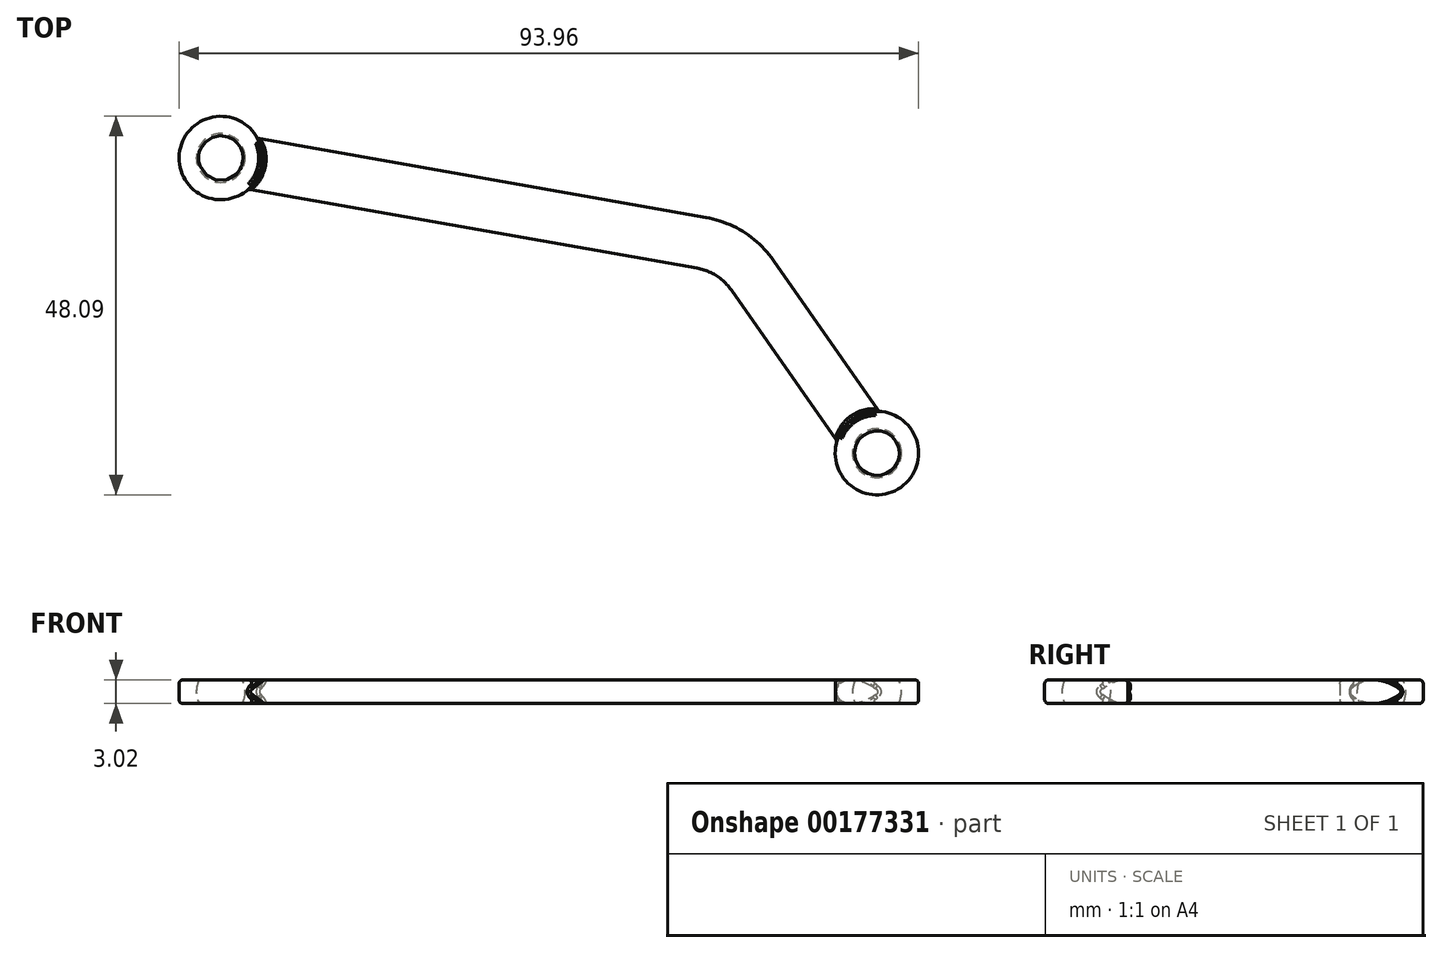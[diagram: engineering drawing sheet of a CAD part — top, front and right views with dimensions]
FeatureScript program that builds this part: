
annotation { "Feature Type Name" : "Feature", "Feature Type Description" : "" }
export const myFeature = defineFeature(function(context is Context, id is Id, definition is map)
    precondition{}
    {
        {
            var Q0;
            Q0=qCreatedBy(makeId("Top.planeOp"),FACE);
            var sketch = newSketch(context, id + "F0", { "sketchPlane" : qUnion([Q0])});
            skLineSegment(sketch, "E0", {"start": v(0, 0) * mm, "end": v(-15.83, 22.6) * mm});
            skLineSegment(sketch, "E1", {"start": v(-22.28, 26.72) * mm, "end": v(-83.36, 37.49) * mm});
            skPoint(sketch, "E2.visualSharp", {"position": v(-18.2, 26) * mm});
            skArc(sketch, "E2.filletArc", {"start": v(-15.83, 22.6) * mm, "mid": v(-18.65, 25.3) * mm, "end": v(-22.28, 26.72) * mm});
            skSolve(sketch);
        }
        {
            var Q0;
            Q0=qCreatedBy(makeId("Top.planeOp"),FACE);
            var sketch = newSketch(context, id + "F1", { "sketchPlane" : qUnion([Q0])});
            skLineSegment(sketch, "E3", {"start": v(-31.75, -22.23) * mm, "end": v(29.07, 20.36) * mm});
            skSolve(sketch);
        }
        {
            var Q0;
            Q0=sQuery(id+"F1.wireOp",EDGE,"E3");
            cPlane(context, id + "F2", {"entities" : qUnion([Q0]), "cplaneType" : CPlaneType.LINE_ANGLE, "offset" : 25 * mm, "angle" : 0 * degree, "width" : 150 * mm, "height" : 150 * mm});
        }
        {
            var Q0;
            Q0=qCreatedBy(id+"F2.planeOp",FACE);
            var sketch = newSketch(context, id + "F3", { "sketchPlane" : qUnion([Q0])});
            skArc(sketch, "E4", {"start": v(3.5, 0) * mm, "mid": v(0, 1.5) * mm, "end": v(-3.5, 0) * mm});
            skArc(sketch, "E5.MirrorCS", {"start": v(3.5, 0) * mm, "mid": v(0, -1.5) * mm, "end": v(-3.5, 0) * mm});
            skSolve(sketch);
        }
        {
            var Q0;
            Q0=makeQuery(id+"F3.imprint","IMPRINT",FACE,{"disambiguationData":[TD([[makeQuery(id+"F3.imprint","IMPRINT",EDGE,{"derivedFrom":sQuery(id+"F3.wireOp",EDGE,"E4")}),1.0]])]});
            var Q1;
            Q1=sQuery(id+"F0.wireOp",EDGE,"E0");
            var Q2;
            Q2=sQuery(id+"F0.wireOp",EDGE,"E2.filletArc");
            var Q3;
            Q3=sQuery(id+"F0.wireOp",EDGE,"E1");
            sweep(context, id + "F4", {"profiles" : qUnion([Q0]), "path" : qUnion([Q1, Q2, Q3])});
        }
        {
            var Q0;
            Q0=qCreatedBy(makeId("Top.planeOp"),FACE);
            var sketch = newSketch(context, id + "F5", { "sketchPlane" : qUnion([Q0])});
            skCircle(sketch, "E6", {"center": v(0, 0) * mm, "radius": 5.3 * mm});
            skCircle(sketch, "E7", {"center": v(-83.36, 37.49) * mm, "radius": 5.3 * mm});
            skSolve(sketch);
        }
        {
            var Q0;
            Q0 = qSketchRegion(id + "F5", true);
            extrude(context, id + "F6", {"entities" : qUnion([Q0]), "operationType" : NewBodyOperationType.ADD, "depth" : 3 * mm, "offsetDistance" : 25 * mm, "symmetric" : true});
        }
        {
            var Q0;
            Q0=qCreatedBy(id+"F2.planeOp",FACE);
            var sketch = newSketch(context, id + "F7", { "sketchPlane" : qUnion([Q0])});
            skLineSegment(sketch, "E8", {"start": v(0, 3.1) * mm, "end": v(0, -3.1) * mm});
            skArc(sketch, "E9", {"start": v(0, 3.1) * mm, "mid": v(-3.1, 0) * mm, "end": v(0, -3.1) * mm});
            skSolve(sketch);
        }
        {
            var Q0;
            Q0 = qSketchRegion(id + "F7", true);
            var Q1;
            Q1=sQuery(id+"F7.wireOp",EDGE,"E8");
            revolve(context, id + "F8", {"operationType" : NewBodyOperationType.REMOVE, "surfaceOperationType" : NewSurfaceOperationType.NEW, "entities" : qUnion([Q0]), "axis" : qUnion([Q1]), "revolveType" : RevolveType.FULL, "oppositeDirection" : true});
        }
        {
            var Q0;
            Q0=makeQuery(id+"F6.opExtrude","CAP_FACE",FACE,{"disambiguationData":[OSD([sQuery(id+"F5.wireOp",EDGE,"E7")])],"isStart":false});
            var sketch = newSketch(context, id + "F9", { "sketchPlane" : qUnion([Q0])});
            skLineSegment(sketch, "E10", {"start": v(-83.36, 42.79) * mm, "end": v(-83.36, 32.19) * mm});
            skPoint(sketch, "E11", {"position": v(-83.36, 37.49) * mm});
            skSolve(sketch);
        }
        {
            var Q0;
            Q0=sQuery(id+"F9.wireOp",EDGE,"E10");
            cPlane(context, id + "F10", {"entities" : qUnion([Q0]), "cplaneType" : CPlaneType.LINE_ANGLE, "offset" : 25 * mm, "angle" : 90 * degree, "width" : 150 * mm, "height" : 150 * mm});
        }
        {
            var Q0;
            Q0=qCreatedBy(id+"F10.planeOp",FACE);
            var sketch = newSketch(context, id + "F11", { "sketchPlane" : qUnion([Q0])});
            skLineSegment(sketch, "E12", {"start": v(37.49, 3.1) * mm, "end": v(37.49, -3.1) * mm});
            skArc(sketch, "E13", {"start": v(37.49, -3.1) * mm, "mid": v(40.59, 0) * mm, "end": v(37.49, 3.1) * mm});
            skSolve(sketch);
        }
        {
            var Q0;
            Q0 = qSketchRegion(id + "F11", true);
            var Q1;
            Q1=sQuery(id+"F11.wireOp",EDGE,"E12");
            revolve(context, id + "F12", {"operationType" : NewBodyOperationType.REMOVE, "surfaceOperationType" : NewSurfaceOperationType.NEW, "entities" : qUnion([Q0]), "axis" : qUnion([Q1]), "revolveType" : RevolveType.FULL, "oppositeDirection" : true});
        }
        {
            var Q0;
            Q0=makeQuery(id+"F6.opExtrude","SWEPT_FACE",FACE,{"disambiguationData":[OSD([sQuery(id+"F5.wireOp",EDGE,"E7")])]});
            var Q1;
            Q1=makeQuery(id+"F6.opExtrude","SWEPT_FACE",FACE,{"disambiguationData":[OSD([sQuery(id+"F5.wireOp",EDGE,"E6")])]});
            var Q2;
            Q2=makeQuery(id+"F4.opSweep","SWEPT_FACE",FACE,{"disambiguationData":[OSD([sQuery(id+"F0.wireOp",EDGE,"E0"),sQuery(id+"F3.wireOp",EDGE,"E4")])]});
            var Q3;
            Q3=makeQuery(id+"F4.opSweep","SWEPT_FACE",FACE,{"disambiguationData":[OSD([sQuery(id+"F0.wireOp",EDGE,"E2.filletArc"),sQuery(id+"F3.wireOp",EDGE,"E4")])]});
            var Q4;
            Q4=makeQuery(id+"F4.opSweep","SWEPT_FACE",FACE,{"disambiguationData":[OSD([sQuery(id+"F0.wireOp",EDGE,"E1"),sQuery(id+"F3.wireOp",EDGE,"E4")])]});
            fillet(context, id + "F13", {"entities" : qUnion([Q0, Q1, Q2, Q3, Q4]), "tangentPropagation" : true, "radius" : 0.5 * mm, "defaultsChanged" : false, "vertexSettings" : [], "allowEdgeOverflow" : false});
        }
        {
            var Q0;
            Q0=makeQuery(id+"F12.boolean.opBoolean","COPY",FACE,{"derivedFrom":makeQuery(id+"F12.opRevolve","SWEPT_FACE",FACE,{"disambiguationData":[OSD([sQuery(id+"F11.wireOp",EDGE,"E13")])]})});
            var Q1;
            Q1=makeQuery(id+"F8.boolean.opBoolean","COPY",FACE,{"derivedFrom":makeQuery(id+"F8.opRevolve","SWEPT_FACE",FACE,{"disambiguationData":[OSD([sQuery(id+"F7.wireOp",EDGE,"E9")])]})});
            fillet(context, id + "F14", {"entities" : qUnion([Q0, Q1]), "tangentPropagation" : true, "radius" : 0.2 * mm, "defaultsChanged" : true, "vertexSettings" : [], "allowEdgeOverflow" : false});
        }
    });
